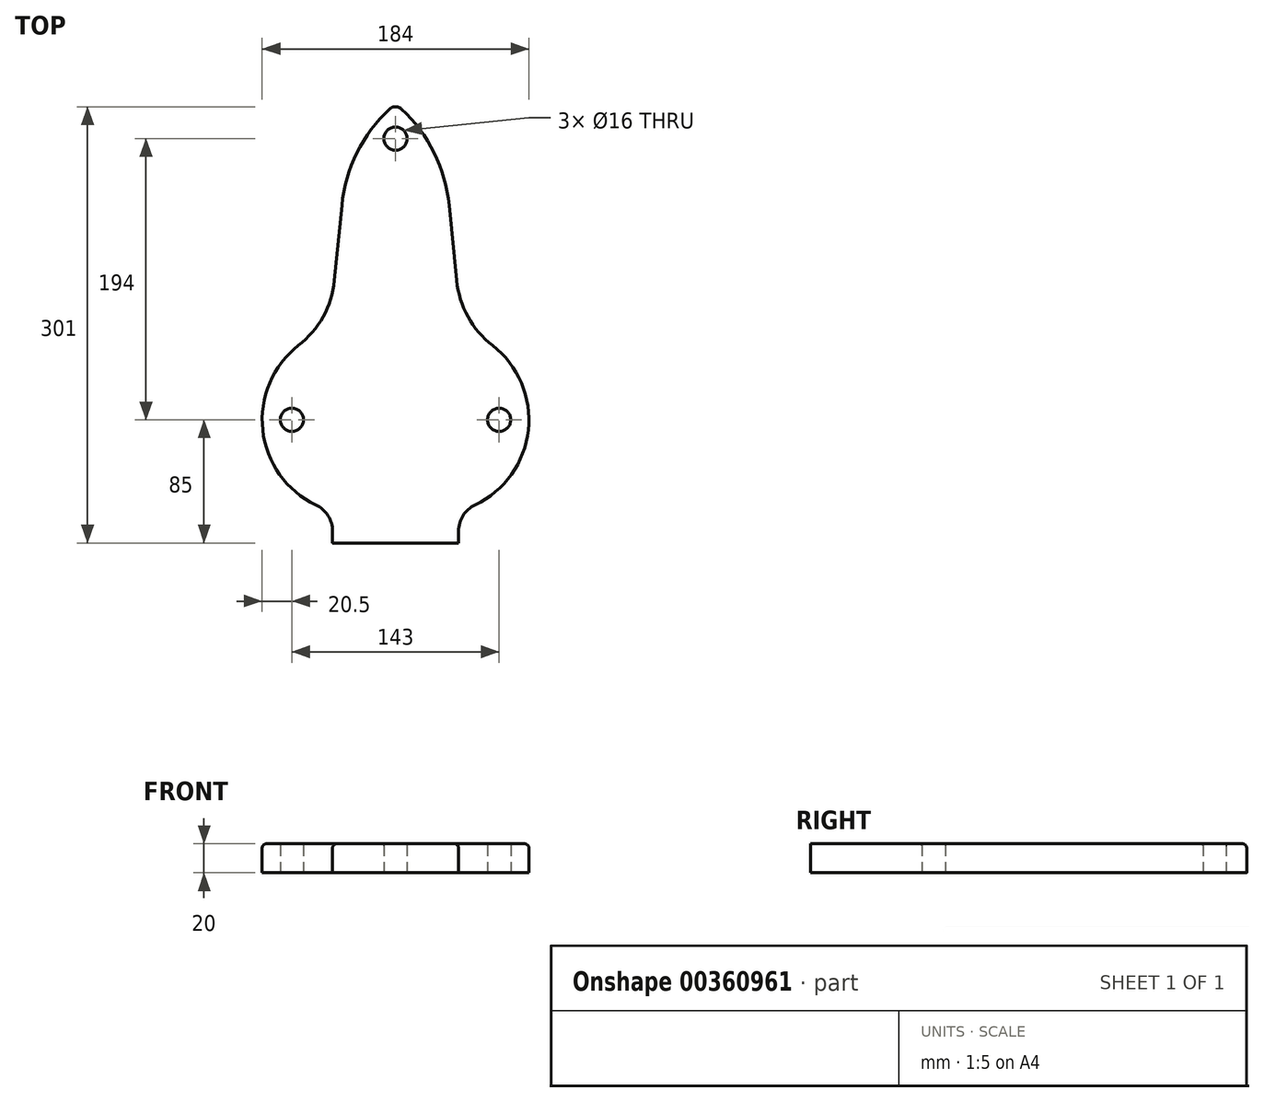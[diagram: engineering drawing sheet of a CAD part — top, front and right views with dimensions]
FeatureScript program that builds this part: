
annotation { "Feature Type Name" : "Feature", "Feature Type Description" : "" }
export const myFeature = defineFeature(function(context is Context, id is Id, definition is map)
    precondition{}
    {
        {
            var Q0;
            Q0=qCreatedBy(makeId("Top.planeOp"),FACE);
            var sketch = newSketch(context, id + "F0", { "sketchPlane" : qUnion([Q0])});
            skLineSegment(sketch, "E0", {"start": v(0, -85) * mm, "end": v(43.5, -85) * mm});
            skLineSegment(sketch, "E1", {"start": v(43.5, -85) * mm, "end": v(43.5, -76.76) * mm});
            skCircle(sketch, "E2", {"center": v(71.5, 0) * mm, "radius": 8 * mm});
            skCircle(sketch, "E3", {"center": v(0, 194) * mm, "radius": 8 * mm});
            skPoint(sketch, "E4", {"position": v(0, 98) * mm});
            skPoint(sketch, "E5", {"position": v(0, 148) * mm});
            skPoint(sketch, "E6", {"position": v(37, 148) * mm});
            skPoint(sketch, "E7", {"position": v(42, 98) * mm});
            skLineSegment(sketch, "E8", {"start": v(37, 148) * mm, "end": v(42.19, 96.1) * mm});
            skArc(sketch, "E9", {"start": v(54.91, -58.7) * mm, "mid": v(91.62, -7.06) * mm, "end": v(66.93, 51.29) * mm});
            skArc(sketch, "E10.filletArc", {"start": v(54.91, -58.7) * mm, "mid": v(46.6, -66.08) * mm, "end": v(43.5, -76.76) * mm});
            skArc(sketch, "E11.filletArc", {"start": v(42.19, 96.1) * mm, "mid": v(49.96, 71.16) * mm, "end": v(66.93, 51.29) * mm});
            skPoint(sketch, "E12", {"position": v(0, 210) * mm});
            skArc(sketch, "E13", {"start": v(4.1, 214.39) * mm, "mid": v(0, 216) * mm, "end": v(-4.1, 214.39) * mm});
            skArc(sketch, "E14", {"start": v(37, 148) * mm, "mid": v(26.6, 184.2) * mm, "end": v(4.1, 214.39) * mm});
            skLineSegment(sketch, "E15.MirrorCS", {"start": v(-37, 148) * mm, "end": v(-42.19, 96.1) * mm});
            skArc(sketch, "E16.MirrorCS", {"start": v(-37, 148) * mm, "mid": v(-26.6, 184.2) * mm, "end": v(-4.1, 214.39) * mm});
            skArc(sketch, "E17.MirrorCS", {"start": v(-42.19, 96.1) * mm, "mid": v(-49.96, 71.16) * mm, "end": v(-66.93, 51.29) * mm});
            skCircle(sketch, "E18.MirrorC", {"center": v(-71.5, 0) * mm, "radius": 8 * mm});
            skArc(sketch, "E19.MirrorCS", {"start": v(-54.91, -58.7) * mm, "mid": v(-91.62, -7.06) * mm, "end": v(-66.93, 51.29) * mm});
            skArc(sketch, "E20.MirrorCS", {"start": v(-54.91, -58.7) * mm, "mid": v(-46.6, -66.08) * mm, "end": v(-43.5, -76.76) * mm});
            skLineSegment(sketch, "E21.MirrorCS", {"start": v(0, -85) * mm, "end": v(-43.5, -85) * mm});
            skLineSegment(sketch, "E22.MirrorCS", {"start": v(-43.5, -85) * mm, "end": v(-43.5, -76.76) * mm});
            skSolve(sketch);
        }
        {
            var Q0;
            Q0=makeQuery(id+"F0.imprint","IMPRINT",FACE,{"disambiguationData":[TD([[makeQuery(id+"F0.imprint","IMPRINT",EDGE,{"derivedFrom":sQuery(id+"F0.wireOp",EDGE,"E0")}),1.0]])]});
            extrude(context, id + "F1", {"entities" : qUnion([Q0]), "depth" : 20 * mm, "offsetDistance" : 25 * mm});
        }
        {
            var Q0;
            Q0=makeQuery(id+"F1.opExtrude","CAP_EDGE",EDGE,{"disambiguationData":[OSD([sQuery(id+"F0.wireOp",EDGE,"E8")])],"isStart":false});
            fillet(context, id + "F2", {"entities" : qUnion([Q0]), "radius" : 3 * mm, "tangentPropagation" : true, "allowEdgeOverflow" : false});
        }
        {
            var Q0;
            Q0=makeQuery(id+"F1.opExtrude","CAP_EDGE",EDGE,{"disambiguationData":[OSD([sQuery(id+"F0.wireOp",EDGE,"E3")])],"isStart":false});
            var Q1;
            Q1=makeQuery(id+"F1.opExtrude","CAP_EDGE",EDGE,{"disambiguationData":[OSD([sQuery(id+"F0.wireOp",EDGE,"E18.MirrorC")])],"isStart":false});
            var Q2;
            Q2=makeQuery(id+"F1.opExtrude","CAP_EDGE",EDGE,{"disambiguationData":[OSD([sQuery(id+"F0.wireOp",EDGE,"E2")])],"isStart":false});
            fillet(context, id + "F3", {"entities" : qUnion([Q0, Q1, Q2]), "radius" : 1 * mm, "tangentPropagation" : true, "allowEdgeOverflow" : false});
        }
    });
